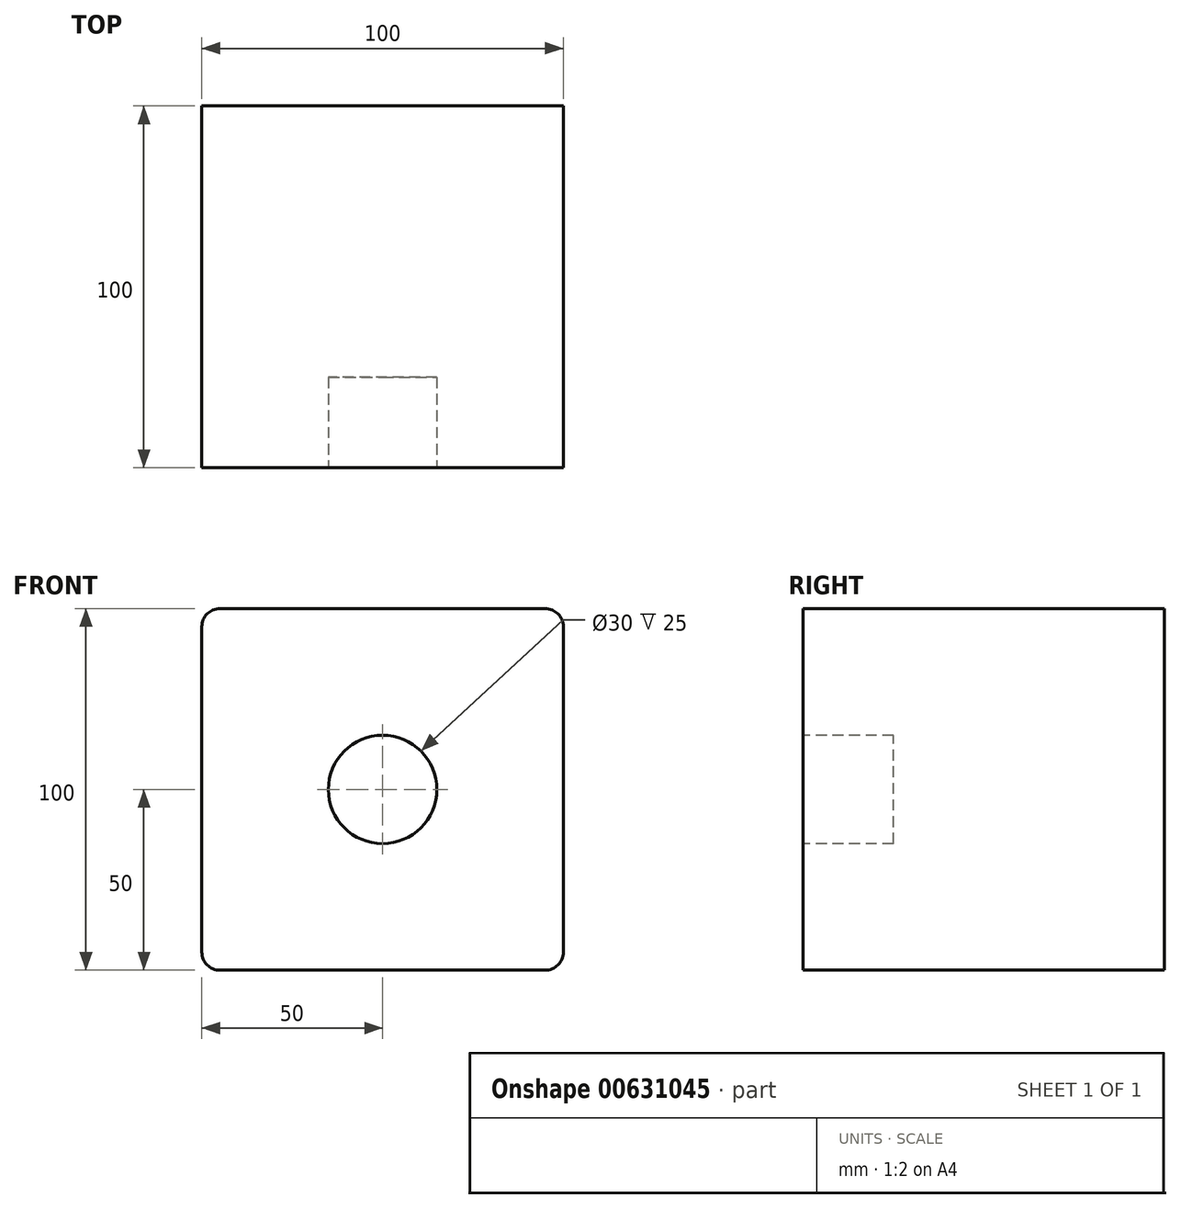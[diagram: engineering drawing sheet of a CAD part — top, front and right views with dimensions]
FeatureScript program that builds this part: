
annotation { "Feature Type Name" : "Feature", "Feature Type Description" : "" }
export const myFeature = defineFeature(function(context is Context, id is Id, definition is map)
    precondition{}
    {
        {
            var Q0;
            Q0=qCreatedBy(makeId("Front.planeOp"),FACE);
            var sketch = newSketch(context, id + "F0", { "sketchPlane" : qUnion([Q0])});
            skLineSegment(sketch, "E0.bottom", {"start": v(45, -50) * mm, "end": v(-45, -50) * mm});
            skLineSegment(sketch, "E0.top", {"start": v(45, 50) * mm, "end": v(-45, 50) * mm});
            skLineSegment(sketch, "E0.left", {"start": v(50, -45) * mm, "end": v(50, 45) * mm});
            skLineSegment(sketch, "E0.right", {"start": v(-50, -45) * mm, "end": v(-50, 45) * mm});
            skPoint(sketch, "E0.middle", {"position": v(0, 0) * mm});
            skPoint(sketch, "E1.visualSharp", {"position": v(-50, 50) * mm});
            skArc(sketch, "E1.filletArc", {"start": v(-45, 50) * mm, "mid": v(-48.54, 48.54) * mm, "end": v(-50, 45) * mm});
            skPoint(sketch, "E2.visualSharp", {"position": v(50, 50) * mm});
            skArc(sketch, "E2.filletArc", {"start": v(50, 45) * mm, "mid": v(48.54, 48.54) * mm, "end": v(45, 50) * mm});
            skPoint(sketch, "E3.visualSharp", {"position": v(50, -50) * mm});
            skArc(sketch, "E3.filletArc", {"start": v(45, -50) * mm, "mid": v(48.54, -48.54) * mm, "end": v(50, -45) * mm});
            skPoint(sketch, "E4.visualSharp", {"position": v(-50, -50) * mm});
            skArc(sketch, "E4.filletArc", {"start": v(-50, -45) * mm, "mid": v(-48.54, -48.54) * mm, "end": v(-45, -50) * mm});
            skSolve(sketch);
        }
        {
            var Q0;
            Q0 = qSketchRegion(id + "F0", true);
            extrude(context, id + "F1", {"entities" : qUnion([Q0]), "oppositeDirection" : true, "depth" : 100 * mm, "offsetDistance" : 25 * mm});
        }
        {
            var Q0;
            Q0=makeQuery(id+"F1.opExtrude","CAP_FACE",FACE,{"disambiguationData":[OSD([sQuery(id+"F0.wireOp",EDGE,"E0.bottom"),sQuery(id+"F0.wireOp",EDGE,"E0.top"),sQuery(id+"F0.wireOp",EDGE,"E0.left"),sQuery(id+"F0.wireOp",EDGE,"E0.right"),sQuery(id+"F0.wireOp",EDGE,"E1.filletArc"),sQuery(id+"F0.wireOp",EDGE,"E2.filletArc"),sQuery(id+"F0.wireOp",EDGE,"E3.filletArc"),sQuery(id+"F0.wireOp",EDGE,"E4.filletArc")])],"isStart":true});
            var sketch = newSketch(context, id + "F2", { "sketchPlane" : qUnion([Q0])});
            skCircle(sketch, "E5", {"center": v(0, 0) * mm, "radius": 15 * mm});
            skSolve(sketch);
        }
        {
            var Q0;
            Q0 = qSketchRegion(id + "F2", true);
            extrude(context, id + "F3", {"entities" : qUnion([Q0]), "operationType" : NewBodyOperationType.REMOVE, "oppositeDirection" : true, "depth" : 25 * mm, "offsetDistance" : 25 * mm});
        }
    });
